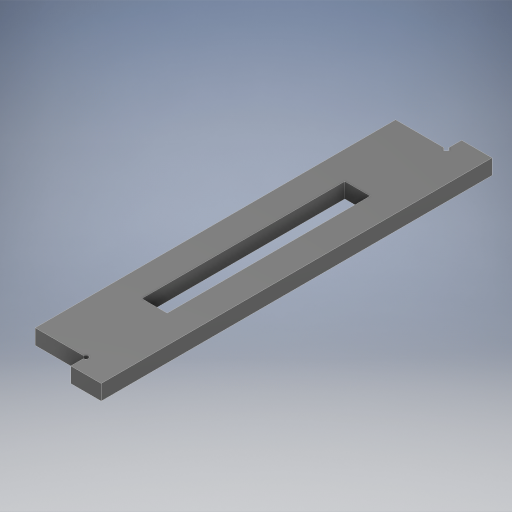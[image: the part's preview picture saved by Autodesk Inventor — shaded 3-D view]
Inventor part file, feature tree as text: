
AUTODESK INVENTOR PART (.ipt)
format: ipt  version: 2024 (Build 280153000, 153)  size: 285,184 bytes
history: native  units: in
note: dims shown in document units (in); Inventor stores cm internally (conversion verified against a paired STEP export)
features: other x4, extrude x3, sketch x3, projected_geometry x1
ambient origin geometry x4: Origin, X Axis, Y Axis, Z Axis
bodies: Body1 (feature_tree)
feature tree (11):
  other  "솔리드1"
  extrude  "돌출1"  Depth=1.2598in
  extrude  "돌출2"  Depth=5.5906in
  extrude  "돌출3"  Depth=0.4724in
  other  "우측면도"
  other  "평면도"
  other  "정면도"
  sketch  "스케치1"
  sketch  "스케치2"
  sketch  "스케치3"
  projected_geometry  "투영된 루프1"
